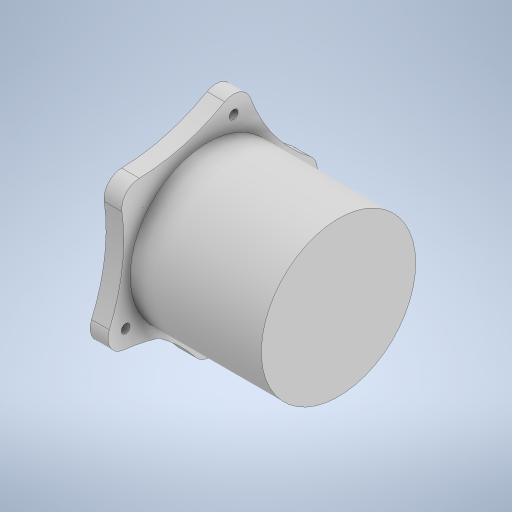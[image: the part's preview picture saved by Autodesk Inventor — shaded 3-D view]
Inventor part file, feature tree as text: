
AUTODESK INVENTOR PART (.ipt)
format: ipt  version: 2023 (Build 270158000, 158)  size: 325,120 bytes
history: native  units: mm
features: extrude x4, sketch x4, other x1, fillet x1
ambient origin geometry x8: Origin, YZ Plane, XZ Plane, XY Plane, X Axis, Y Axis, Z Axis, Center Point
bodies: Body1 (feature_tree)
feature tree (10):
  other  "Твердое тело1"
  extrude  "Выдавливание1"  Depth=10.0mm TaperAngle=0.0deg
  extrude  "Выдавливание2"  Depth=87.0mm
  extrude  "Выдавливание3"  Depth=74.0mm TaperAngle=0.0deg
  extrude  "Выдавливание4"  Depth=70.0mm
  fillet  "Сопряжение1"  Radius=5.0mm
  sketch  "Эскиз1"
  sketch  "Эскиз2"
  sketch  "Эскиз3"
  sketch  "Эскиз4"
